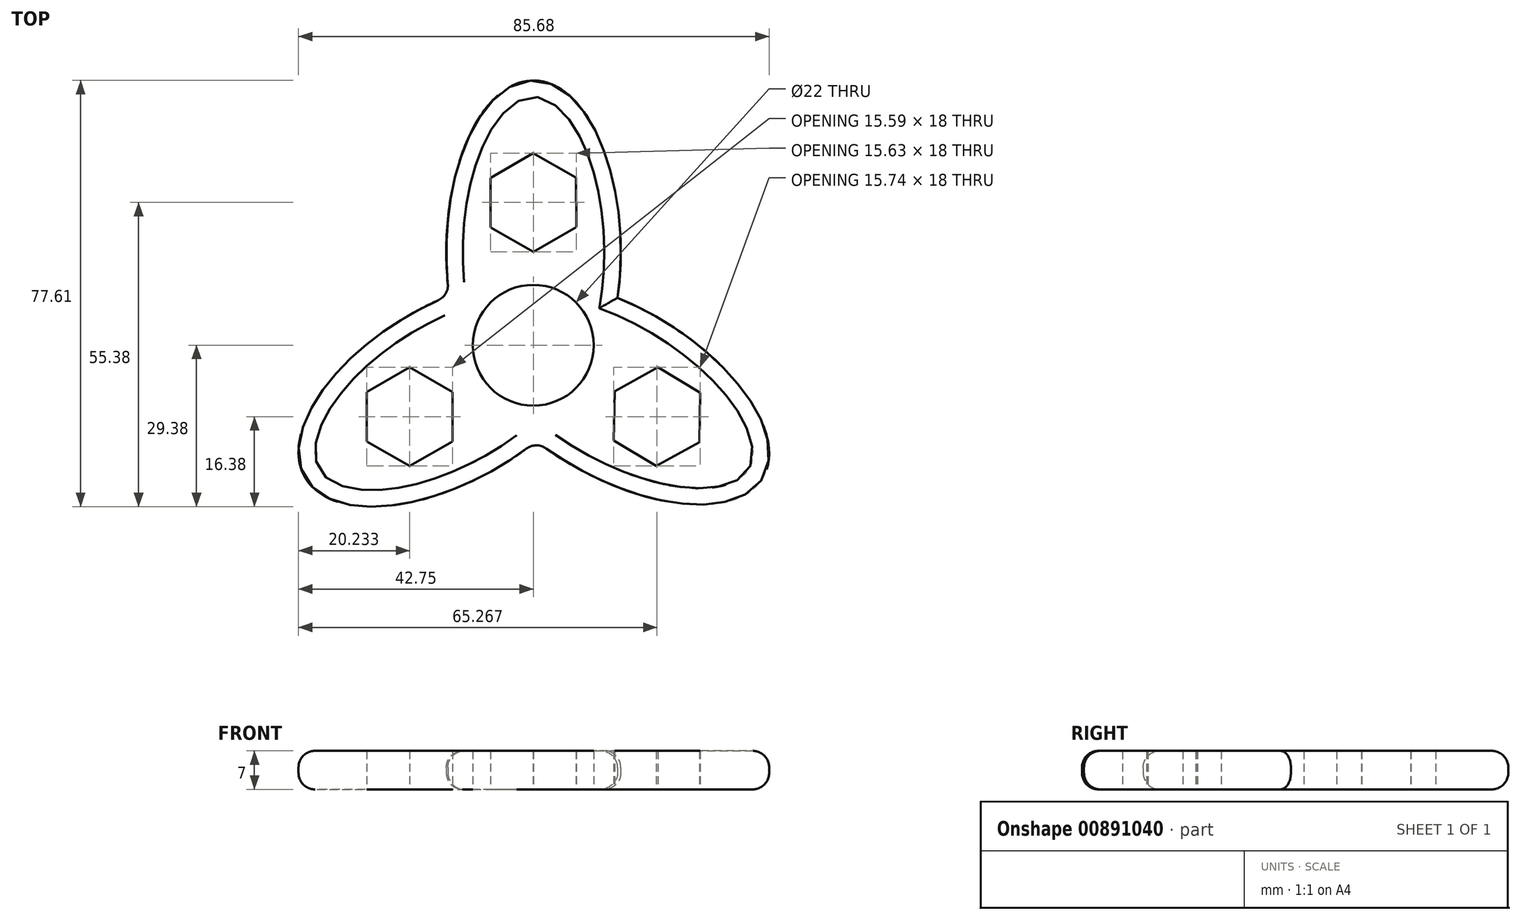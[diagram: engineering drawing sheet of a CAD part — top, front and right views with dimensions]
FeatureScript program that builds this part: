
annotation { "Feature Type Name" : "Feature", "Feature Type Description" : "" }
export const myFeature = defineFeature(function(context is Context, id is Id, definition is map)
    precondition{}
    {
        {
            var Q0;
            Q0=qCreatedBy(makeId("Top.planeOp"),FACE);
            var sketch = newSketch(context, id + "F0", { "sketchPlane" : qUnion([Q0])});
            skCircle(sketch, "E0", {"center": v(0, 0) * mm, "radius": 11 * mm});
            skLineSegment(sketch, "E1", {"start": v(-14.72, -8.5) * mm, "end": v(-22.52, -13) * mm});
            skCircle(sketch, "E2.cCircle", {"center": v(-22.52, -13) * mm, "radius": 9 * mm, "construction": true});
            skLineSegment(sketch, "E2.0", {"start": v(-14.72, -8.5) * mm, "end": v(-14.72, -17.5) * mm});
            skLineSegment(sketch, "E2.1", {"start": v(-14.72, -17.5) * mm, "end": v(-22.52, -22) * mm});
            skLineSegment(sketch, "E2.2", {"start": v(-22.52, -22) * mm, "end": v(-30.31, -17.5) * mm});
            skLineSegment(sketch, "E2.3", {"start": v(-30.31, -17.5) * mm, "end": v(-30.31, -8.5) * mm});
            skLineSegment(sketch, "E2.4", {"start": v(-30.31, -8.5) * mm, "end": v(-22.52, -4) * mm});
            skLineSegment(sketch, "E2.5", {"start": v(-22.52, -4) * mm, "end": v(-14.72, -8.5) * mm});
            skCircle(sketch, "E3.cCircle", {"center": v(22.52, -13) * mm, "radius": 9 * mm, "construction": true});
            skLineSegment(sketch, "E3.0", {"start": v(30.39, -8.63) * mm, "end": v(30.23, -17.63) * mm});
            skLineSegment(sketch, "E3.1", {"start": v(30.23, -17.63) * mm, "end": v(22.36, -22) * mm});
            skLineSegment(sketch, "E3.2", {"start": v(22.36, -22) * mm, "end": v(14.65, -17.37) * mm});
            skLineSegment(sketch, "E3.3", {"start": v(14.65, -17.37) * mm, "end": v(14.8, -8.37) * mm});
            skLineSegment(sketch, "E3.4", {"start": v(14.8, -8.37) * mm, "end": v(22.67, -4) * mm});
            skLineSegment(sketch, "E3.5", {"start": v(22.67, -4) * mm, "end": v(30.39, -8.63) * mm});
            skLineSegment(sketch, "E4", {"start": v(0, 26) * mm, "end": v(0, 0) * mm});
            skEllipticalArc(sketch, "E5", {});
            skCircle(sketch, "E6.cCircle", {"center": v(0, 26) * mm, "radius": 9 * mm, "construction": true});
            skLineSegment(sketch, "E6.0", {"start": v(7.78, 30.53) * mm, "end": v(7.81, 21.53) * mm});
            skLineSegment(sketch, "E6.1", {"start": v(7.81, 21.53) * mm, "end": v(0.04, 17) * mm});
            skLineSegment(sketch, "E6.2", {"start": v(0.04, 17) * mm, "end": v(-7.78, 21.47) * mm});
            skLineSegment(sketch, "E6.3", {"start": v(-7.78, 21.47) * mm, "end": v(-7.81, 30.47) * mm});
            skLineSegment(sketch, "E6.4", {"start": v(-7.81, 30.47) * mm, "end": v(-0.04, 35) * mm});
            skLineSegment(sketch, "E6.5", {"start": v(-0.04, 35) * mm, "end": v(7.78, 30.53) * mm});
            skEllipticalArc(sketch, "E7", {});
            skEllipticalArc(sketch, "E8", {});
            skLineSegment(sketch, "E9.trimOffspring", {"start": v(14.72, -8.5) * mm, "end": v(14.8, -8.54) * mm});
            const initialGuessF0  = {"E5": [-0.01472243186433546, -0.0085, 0.8647071125528175, 0.5022764273789575, 0.03104360915066664, 0.016055243575197945, 1.3004029951274814, 4.995570659336357], "E7": [3.7156459248207166e-05, 0.017000076700463707, 0, -1, 0.031230027195527966, 0.01588471271314451, 1.3004621403439987, 4.969999997674323], "E8": [0.014798549244257848, -0.008368160830635369, -0.864949040586103, 0.5018596987098884, 0.03125558233429243, 0.015529682420978054, 1.3192423712778778, 4.973644579072925]};
            skSetInitialGuess(sketch, initialGuessF0);
            skSolve(sketch);
        }
        {
            var Q0;
            Q0 = qSketchRegion(id + "F0", true);
            extrude(context, id + "F1", {"entities" : qUnion([Q0]), "depth" : 7 * mm, "offsetDistance" : 25 * mm});
        }
        {
            var Q0;
            Q0=makeQuery(id+"F1.opExtrude","CAP_EDGE",EDGE,{"disambiguationData":[OSD([sQuery(id+"F0.wireOp",EDGE,"E5")])],"isStart":false});
            var Q1;
            Q1=makeQuery(id+"F1.opExtrude","CAP_EDGE",EDGE,{"disambiguationData":[OSD([sQuery(id+"F0.wireOp",EDGE,"E7")])],"isStart":false});
            var Q2;
            Q2=makeQuery(id+"F1.opExtrude","CAP_EDGE",EDGE,{"disambiguationData":[OSD([sQuery(id+"F0.wireOp",EDGE,"E8")])],"isStart":false});
            var Q3;
            Q3=makeQuery(id+"F1.opExtrude","CAP_EDGE",EDGE,{"disambiguationData":[OSD([sQuery(id+"F0.wireOp",EDGE,"E8")])],"isStart":true});
            var Q4;
            Q4=makeQuery(id+"F1.opExtrude","SWEPT_FACE",FACE,{"disambiguationData":[OSD([sQuery(id+"F0.wireOp",EDGE,"E5")])]});
            var Q5;
            Q5=makeQuery(id+"F1.opExtrude","CAP_EDGE",EDGE,{"disambiguationData":[OSD([sQuery(id+"F0.wireOp",EDGE,"E7")])],"isStart":true});
            fillet(context, id + "F2", {"entities" : qUnion([Q0, Q1, Q2, Q3, Q4, Q5]), "radius" : 3 * mm, "tangentPropagation" : true, "allowEdgeOverflow" : false});
        }
    });
